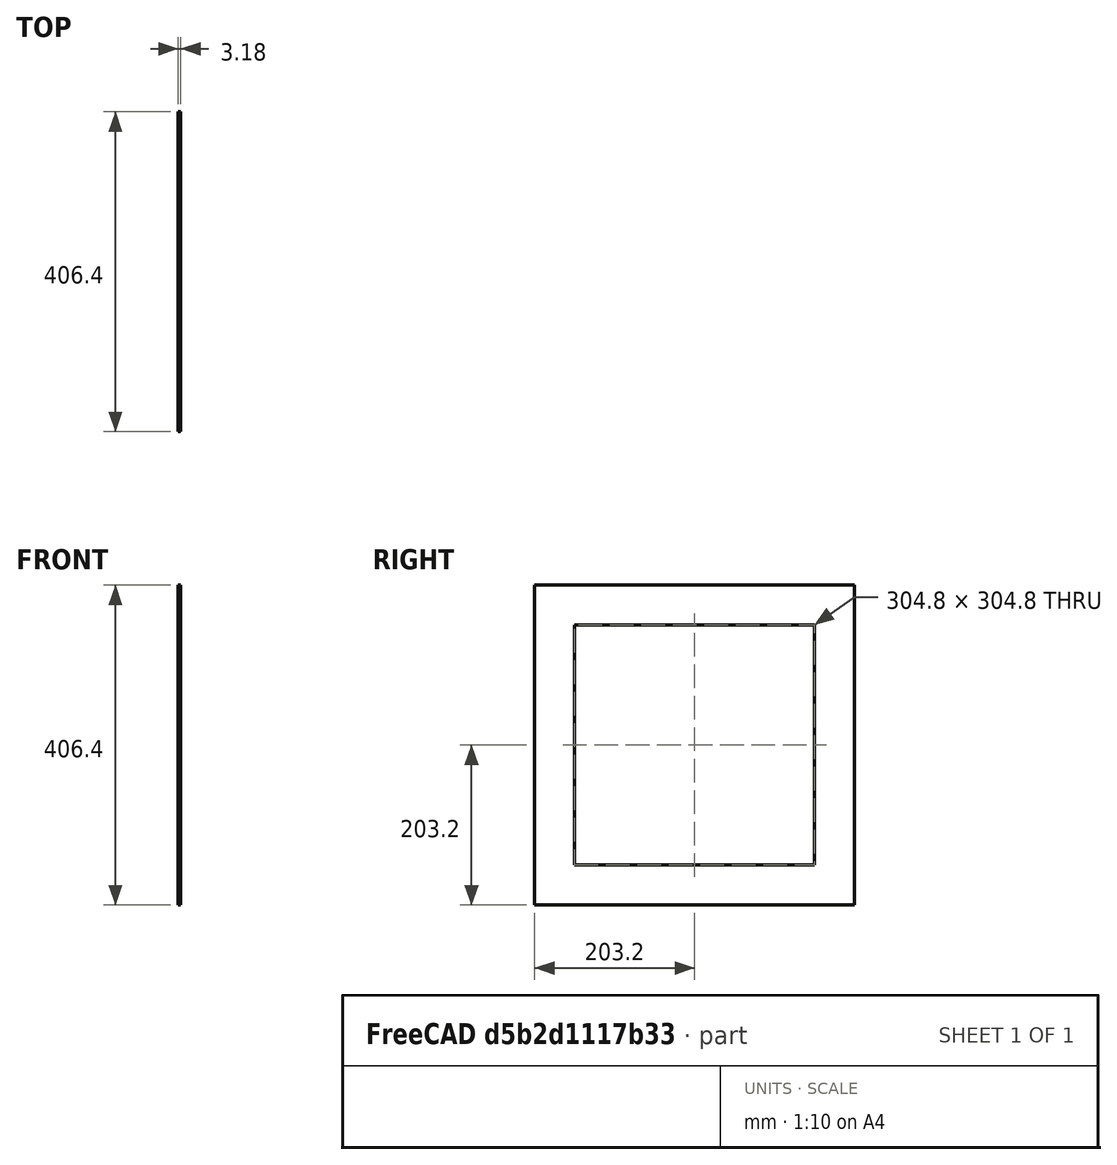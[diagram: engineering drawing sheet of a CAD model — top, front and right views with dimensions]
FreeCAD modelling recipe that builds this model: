
FCSTD DOCUMENT  (FreeCAD 0.16R6707 (Git))
Label: Single Frame 16in
License: CreativeCommons Attribution
LicenseURL: http://creativecommons.org/licenses/by/4.0/
objects: Sketcher::SketchObject×1, PartDesign::Pad×1
note: 3 computed .brp shape members not serialized (recipe doc carries the construction recipe); baked Part::Feature solids carry a one-line shape summary decoded from their .brp

FEATURE [Sketcher::SketchObject] Sketch
  Placement = pos=(0,0,0) rot=(0.57735,0.57735,0.57735;2.0944rad)
  sketch-geometry (8):
    g0: LineSegment StartX=0 StartY=406.4 StartZ=0 EndX=406.4 EndY=406.4 EndZ=0
    g1: LineSegment StartX=406.4 StartY=406.4 StartZ=0 EndX=406.4 EndY=0 EndZ=0
    g2: LineSegment StartX=406.4 StartY=0 StartZ=0 EndX=0 EndY=0 EndZ=0
    g3: LineSegment StartX=0 StartY=0 StartZ=0 EndX=0 EndY=406.4 EndZ=0
    g4: LineSegment StartX=50.8 StartY=355.6 StartZ=0 EndX=355.6 EndY=355.6 EndZ=0
    g5: LineSegment StartX=355.6 StartY=355.6 StartZ=0 EndX=355.6 EndY=50.8 EndZ=0
    g6: LineSegment StartX=355.6 StartY=50.8 StartZ=0 EndX=50.8 EndY=50.8 EndZ=0
    g7: LineSegment StartX=50.8 StartY=50.8 StartZ=0 EndX=50.8 EndY=355.6 EndZ=0
  constraints (23):
    c: Coincident(g0,g1)
    c: Coincident(g1,g2)
    c: Coincident(g2,g3)
    c: Coincident(g3,g0)
    c: Horizontal(g0)
    c: Horizontal(g2)
    c: Vertical(g1)
    c: Vertical(g3)
    c: Equal(g0,g3)
    c: DistanceX(g0,g0) = 406.4
    c: Coincident(g4,g5)
    c: Coincident(g5,g6)
    c: Coincident(g6,g7)
    c: Coincident(g7,g4)
    c: Horizontal(g4)
    c: Horizontal(g6)
    c: Vertical(g5)
    c: Vertical(g7)
    c: DistanceX(g0,g4) = 50.8
    c: Equal(g4,g7)
    c: Coincident(g2,g-1)
    c: DistanceY(g4,g0) = 50.8
    c: DistanceX(g4,g4) = 304.8
FEATURE [PartDesign::Pad] Pad  label="Single Frame 16in"
  Length = 3.175
  Length2 = 100
  Midplane = true
  Placement = pos=(0,0,0) rot=(0.57735,0.57735,0.57735;2.0944rad)
  Sketch = -> Sketch
  Type = 0
